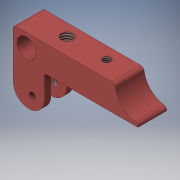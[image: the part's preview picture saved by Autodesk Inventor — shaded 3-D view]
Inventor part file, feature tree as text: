
AUTODESK INVENTOR PART (.ipt)
format: ipt  version: 2016 SP1 (Build 200210100, 210)  size: 297,472 bytes
history: native  units: mm
features: sketch x7, hole x5, fillet x4, extrude x2
ambient origin geometry x8: Origin, YZ Plane, XZ Plane, XY Plane, X Axis, Y Axis, Z Axis, Center Point
bodies: Solid1 (feature_tree)
feature tree (18):
  extrude  "Extrusion1"  Depth=52.0mm
  hole  "Hole1"  [1 undecoded]
  hole  "Hole2"  [1 undecoded]
  extrude  "Extrusion2"  Depth=6.5mm
  hole  "Hole3"  [1 undecoded]
  hole  "Hole4"  [1 undecoded]
  hole  "Hole5"  [1 undecoded]
  fillet  "Fillet1"  Radius=7.0mm
  fillet  "Fillet2"  Radius=32.0mm
  fillet  "Fillet3"  Radius=1.5mm
  fillet  "Fillet4"  Radius=6.5mm
  sketch  "Sketch1"  dims[d0=27.0mm d1=52.0mm]
  sketch  "Sketch2"  dims[d2=11.0mm d3=39.0mm]
  sketch  "Sketch3"  dims[d4=12.0mm d5=0.0mm d6=5.5mm]
  sketch  "Sketch4"  dims[d7=5.5mm]
  sketch  "Sketch5"  dims[d8=3.5mm d9=6.0mm d10=8.0mm d11=6.5mm d12=90.0deg d13=8.0mm d14=20.594885mm d15=8.0mm]
  sketch  "Sketch6"  dims[d16=5.5mm]
  sketch  "Sketch7"  dims[d17=2.459mm d18=6.0mm d19=8.0mm d20=6.5mm d21=90.0deg d22=8.8mm d23=20.594885mm d26=12.0mm d27=0.0mm d28=7.0mm d29=15.5mm d30=4.917mm d31=15.0mm d32=8.0mm d33=6.5mm d34=90.0deg d35=17.1mm d36=20.594885mm d37=7.0mm d38=32.0mm d39=3.242mm d40=8.0mm d41=8.0mm d42=6.5mm d43=90.0deg d44=11.8mm d45=20.594885mm d46=19.0mm d47=8.0mm d48=8.0mm d49=6.5mm d50=90.0deg d51=11.8mm d52=20.594885mm d53=1.5mm d54=6.5mm d55=1.0mm d56=1.0mm d57=16.0mm d58=12.0mm d59=6.6mm d60=2.7mm]
note: 5 required parameter values undecoded (feature->parameter linkage not recoverable at this tier; creation-order binding heuristic only, values carry confidence <= 0.55)
